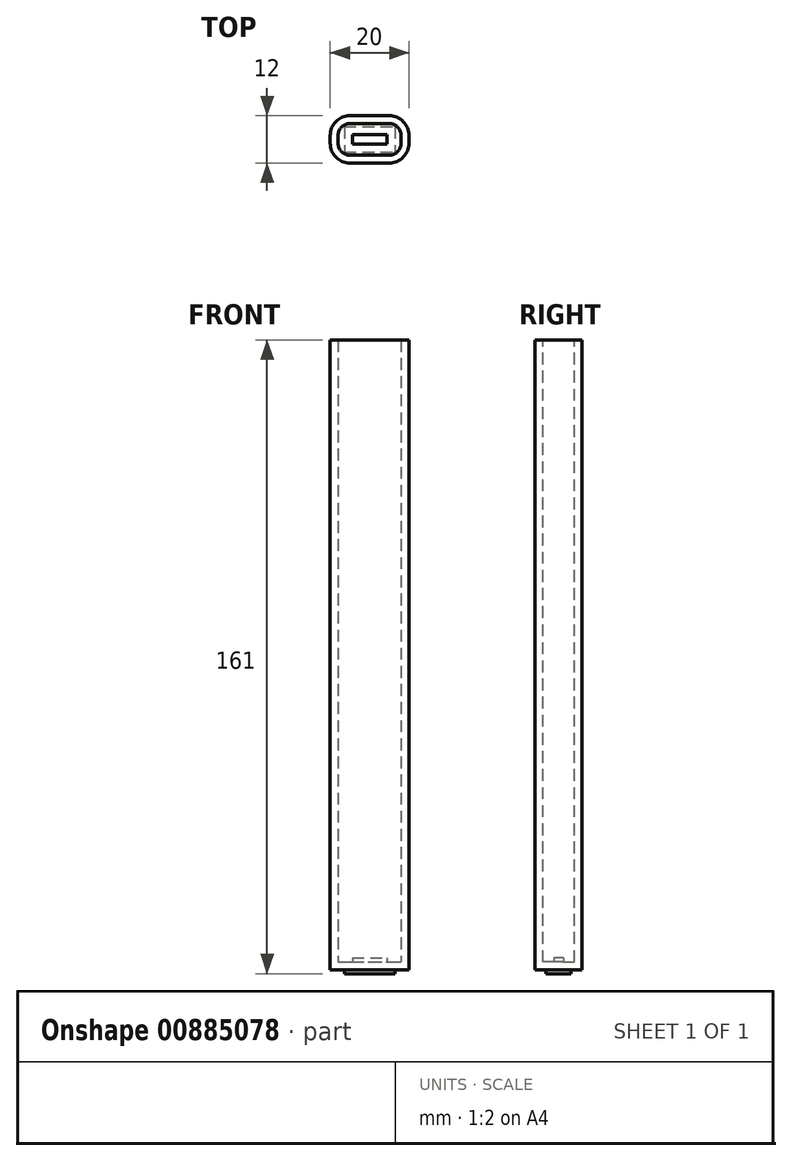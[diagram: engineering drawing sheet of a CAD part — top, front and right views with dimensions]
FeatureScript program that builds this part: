
annotation { "Feature Type Name" : "Feature", "Feature Type Description" : "" }
export const myFeature = defineFeature(function(context is Context, id is Id, definition is map)
    precondition{}
    {
        {
            var Q0;
            Q0=qCreatedBy(makeId("Top.planeOp"),FACE);
            var sketch = newSketch(context, id + "F0", { "sketchPlane" : qUnion([Q0])});
            skLineSegment(sketch, "E0.bottom", {"start": v(-6.4, 3.2) * mm, "end": v(6.4, 3.2) * mm});
            skLineSegment(sketch, "E0.top", {"start": v(-6.4, -3.2) * mm, "end": v(6.4, -3.2) * mm});
            skLineSegment(sketch, "E0.left", {"start": v(-6.4, 3.2) * mm, "end": v(-6.4, -3.2) * mm});
            skLineSegment(sketch, "E0.right", {"start": v(6.4, 3.2) * mm, "end": v(6.4, -3.2) * mm});
            skPoint(sketch, "E0.middle", {"position": v(0, 0) * mm});
            skLineSegment(sketch, "E1.bottom", {"start": v(-10, 6) * mm, "end": v(10, 6) * mm});
            skLineSegment(sketch, "E1.top", {"start": v(-10, -6) * mm, "end": v(10, -6) * mm});
            skLineSegment(sketch, "E1.left", {"start": v(-10, 6) * mm, "end": v(-10, -6) * mm});
            skLineSegment(sketch, "E1.right", {"start": v(10, 6) * mm, "end": v(10, -6) * mm});
            skSolve(sketch);
        }
        {
            var Q0;
            Q0=makeQuery(id+"F0.imprint","IMPRINT",FACE,{"disambiguationData":[TD([[makeQuery(id+"F0.imprint","IMPRINT",EDGE,{"derivedFrom":sQuery(id+"F0.wireOp",EDGE,"E0.bottom")}),-1.0]])]});
            extrude(context, id + "F1", {"entities" : qUnion([Q0]), "oppositeDirection" : true, "depth" : 1 * mm, "offsetDistance" : 25 * mm});
        }
        {
            var Q0;
            Q0=makeQuery(id+"F0.imprint","IMPRINT",FACE,{"disambiguationData":[TD([[makeQuery(id+"F0.imprint","IMPRINT",EDGE,{"derivedFrom":sQuery(id+"F0.wireOp",EDGE,"E0.bottom")}),1.0]])]});
            var Q1;
            Q1=makeQuery(id+"F0.imprint","IMPRINT",FACE,{"disambiguationData":[TD([[makeQuery(id+"F0.imprint","IMPRINT",EDGE,{"derivedFrom":sQuery(id+"F0.wireOp",EDGE,"E0.bottom")}),-1.0]])]});
            extrude(context, id + "F2", {"entities" : qUnion([Q0, Q1]), "operationType" : NewBodyOperationType.ADD, "depth" : 160 * mm, "offsetDistance" : 25 * mm});
        }
        {
            var Q0;
            Q0=makeQuery(id+"F2.opExtrude","SWEPT_EDGE",EDGE,{"disambiguationData":[OSD([sQuery(id+"F0.wireOp",EDGE,"E1.top"),sQuery(id+"F0.wireOp",EDGE,"E1.left")])]});
            var Q1;
            Q1=makeQuery(id+"F2.opExtrude","SWEPT_EDGE",EDGE,{"disambiguationData":[OSD([sQuery(id+"F0.wireOp",EDGE,"E1.top"),sQuery(id+"F0.wireOp",EDGE,"E1.right")])]});
            var Q2;
            Q2=makeQuery(id+"F2.opExtrude","SWEPT_EDGE",EDGE,{"disambiguationData":[OSD([sQuery(id+"F0.wireOp",EDGE,"E1.bottom"),sQuery(id+"F0.wireOp",EDGE,"E1.right")])]});
            var Q3;
            Q3=makeQuery(id+"F2.opExtrude","SWEPT_EDGE",EDGE,{"disambiguationData":[OSD([sQuery(id+"F0.wireOp",EDGE,"E1.bottom"),sQuery(id+"F0.wireOp",EDGE,"E1.left")])]});
            fillet(context, id + "F3", {"entities" : qUnion([Q0, Q1, Q2, Q3]), "radius" : 5 * mm, "tangentPropagation" : true, "allowEdgeOverflow" : false});
        }
        {
            var Q0;
            Q0=makeQuery(id+"F2.opExtrude","CAP_FACE",FACE,{"disambiguationData":[OSD([sQuery(id+"F0.wireOp",EDGE,"E1.bottom"),sQuery(id+"F0.wireOp",EDGE,"E1.top"),sQuery(id+"F0.wireOp",EDGE,"E1.left"),sQuery(id+"F0.wireOp",EDGE,"E1.right")])],"isStart":false});
            shell(context, id + "F4", {"entities" : qUnion([Q0]), "thickness" : 2 * mm});
        }
        {
            var Q0;
            Q0=makeQuery(id+"F4.opShell","OFFSET_FACE",FACE,{"disambiguationData":[OSD([sQuery(id+"F0.wireOp",EDGE,"E0.bottom"),sQuery(id+"F0.wireOp",EDGE,"E0.top"),sQuery(id+"F0.wireOp",EDGE,"E0.left"),sQuery(id+"F0.wireOp",EDGE,"E0.right")])]});
            extrude(context, id + "F5", {"entities" : qUnion([Q0]), "operationType" : NewBodyOperationType.ADD, "depth" : 2 * mm, "offsetDistance" : 25 * mm});
        }
    });
